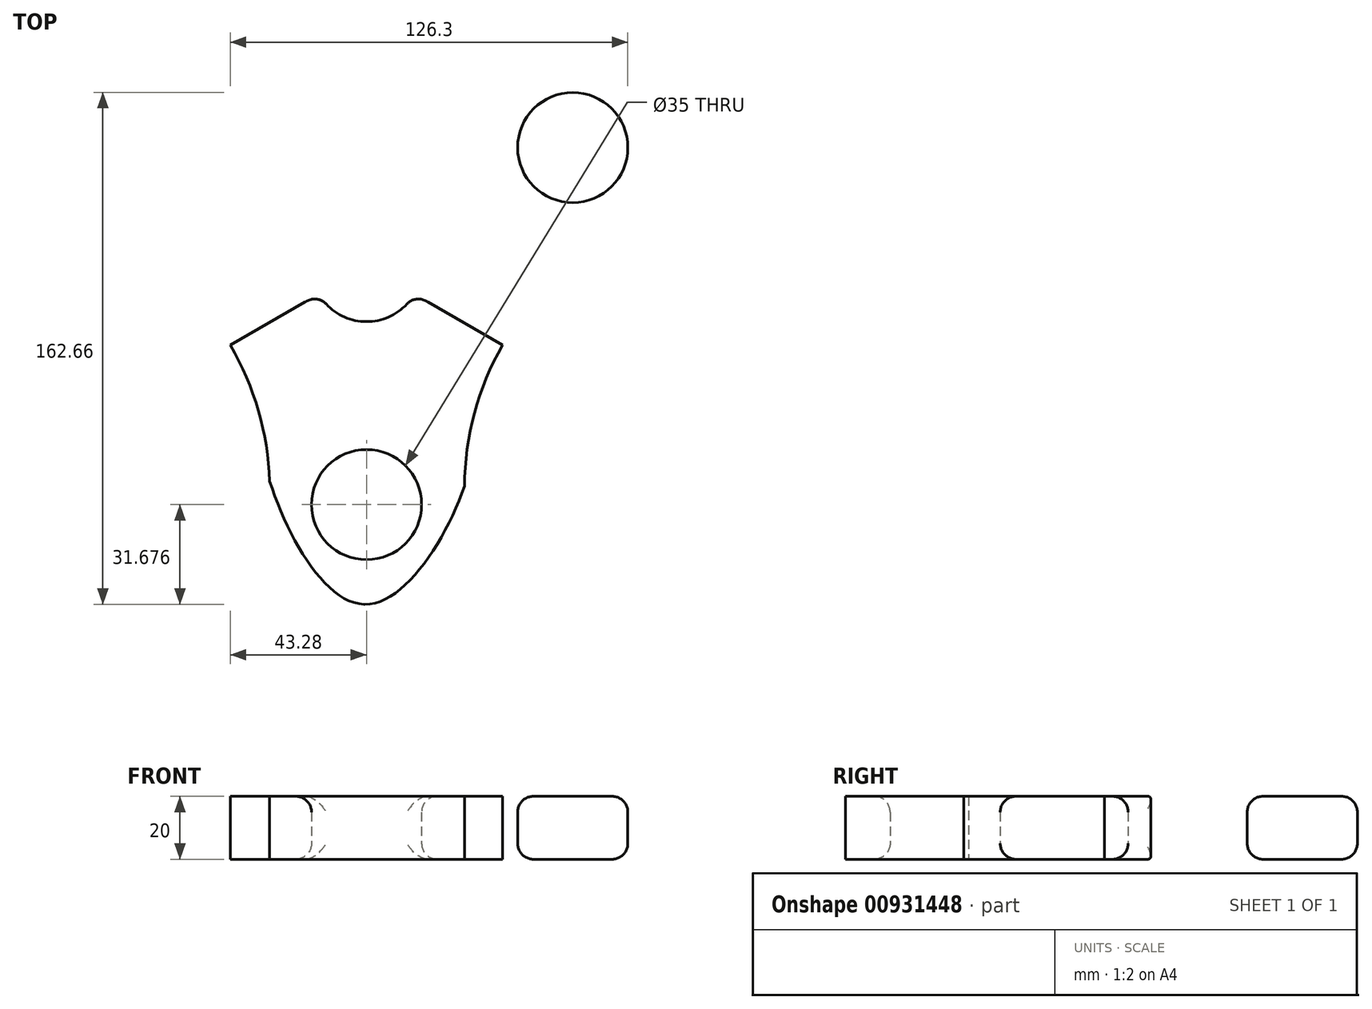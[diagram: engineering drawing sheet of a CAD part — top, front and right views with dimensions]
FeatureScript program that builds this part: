
annotation { "Feature Type Name" : "Feature", "Feature Type Description" : "" }
export const myFeature = defineFeature(function(context is Context, id is Id, definition is map)
    precondition{}
    {
        {
            var Q0;
            Q0=qCreatedBy(makeId("Top.planeOp"),FACE);
            var sketch = newSketch(context, id + "F0", { "sketchPlane" : qUnion([Q0])});
            skCircle(sketch, "E0.MirrorC", {"center": v(-65.69, 37.54) * mm, "radius": 17.5 * mm});
            skCircle(sketch, "E1", {"center": v(0, 0) * mm, "radius": 107.34 * mm});
            skArc(sketch, "E2", {"start": v(-43.65, 60.75) * mm, "mid": v(-92.55, 54.36) * mm, "end": v(-75.97, 7.92) * mm});
            skCircle(sketch, "E3.MirrorC", {"center": v(65.52, 37.83) * mm, "radius": 17.5 * mm});
            skCircle(sketch, "E4", {"center": v(0, 0) * mm, "radius": 17.5 * mm});
            skLineSegment(sketch, "E5", {"start": v(0, 0) * mm, "end": v(0, 50.1) * mm});
            skArc(sketch, "E6.MirrorCS", {"start": v(43.65, 60.75) * mm, "mid": v(92.55, 54.36) * mm, "end": v(75.97, 7.92) * mm});
            skLineSegment(sketch, "E7", {"start": v(0, 0) * mm, "end": v(92.96, -53.67) * mm});
            skLineSegment(sketch, "E8", {"start": v(0, 0) * mm, "end": v(-92.96, -53.67) * mm});
            skArc(sketch, "E9.trimOffspring", {"start": v(-43.38, -25.05) * mm, "mid": v(-57.52, -6.43) * mm, "end": v(-75.97, 7.92) * mm});
            skCircle(sketch, "E10.MirrorC", {"center": v(0, -75.65) * mm, "radius": 17.5 * mm});
            skArc(sketch, "E11", {"start": v(-30.79, -68.18) * mm, "mid": v(-43.65, -24.36) * mm, "end": v(-75.97, 7.92) * mm});
            skArc(sketch, "E12", {"start": v(-43.65, 60.75) * mm, "mid": v(0.28, 50.42) * mm, "end": v(44.14, 61.02) * mm});
            skArc(sketch, "E13", {"start": v(75.97, 7.92) * mm, "mid": v(43.25, -24.97) * mm, "end": v(31.13, -69.75) * mm});
            skArc(sketch, "E14", {"start": v(-30.79, -68.18) * mm, "mid": v(-0.8, -107.33) * mm, "end": v(31.13, -69.75) * mm});
            skFitSpline(sketch, "E15", {"points": [v(-75.97, 7.92) * mm, v(-43.38, -25.05) * mm, v(-30.79, -68.18) * mm, v(-0.8, -107.33) * mm, v(31.13, -69.75) * mm, v(43.38, -25.05) * mm, v(75.97, 7.92) * mm, v(92.96, 53.67) * mm, v(44.14, 61.02) * mm, v(0, 50.1) * mm, v(-43.65, 60.75) * mm, v(-94.93, 50.1) * mm, v(-75.97, 7.92) * mm]});
            skSolve(sketch);
        }
        {
            var Q0;
            {var subQ5=sQuery(id+"F0.wireOp",EDGE,"zdI8FKuQ-oBQZ-7qeJ-rRJp-botCcD2bO7yp");Q0=makeQuery(id+"F0.imprint","IMPRINT",FACE,{"disambiguationData":[TD([[makeQuery(id+"F0.imprint","IMPRINT",EDGE,{"derivedFrom":subQ5}),-1.0]])]});}
            var Q1;
            Q1=makeQuery(id+"F0.imprint","IMPRINT",FACE,{"disambiguationData":[TD([[makeQuery(id+"F0.imprint","IMPRINT",EDGE,{"derivedFrom":sQuery(id+"F0.wireOp",EDGE,"E3.MirrorC")}),1.0]])]});
            var Q2;
            Q2=makeQuery(id+"F0.imprint","IMPRINT",FACE,{"disambiguationData":[TD([[makeQuery(id+"F0.imprint","IMPRINT",EDGE,{"derivedFrom":sQuery(id+"F0.wireOp",EDGE,"E0.MirrorC")}),-1.0]])]});
            var Q3;
            Q3=makeQuery(id+"F0.imprint","IMPRINT",FACE,{"disambiguationData":[TD([[makeQuery(id+"F0.imprint","IMPRINT",EDGE,{"derivedFrom":sQuery(id+"F0.wireOp",EDGE,"E10.MirrorC")}),-1.0]])]});
            extrude(context, id + "F1", {"entities" : qUnion([Q0, Q1, Q2, Q3]), "depth" : 20 * mm, "offsetDistance" : 25 * mm});
        }
        {
            var Q0;
            Q0=makeQuery(id+"F1.opExtrude","SWEPT_FACE",FACE,{"disambiguationData":[OSD([sQuery(id+"F0.wireOp",EDGE,"E0.MirrorC")])]});
            var Q1;
            Q1=makeQuery(id+"F1.opExtrude","SWEPT_FACE",FACE,{"disambiguationData":[OSD([sQuery(id+"F0.wireOp",EDGE,"E4")])]});
            var Q2;
            Q2=makeQuery(id+"F1.opExtrude","SWEPT_FACE",FACE,{"disambiguationData":[OSD([sQuery(id+"F0.wireOp",EDGE,"E3.MirrorC")])]});
            var Q3;
            Q3=makeQuery(id+"F1.opExtrude","SWEPT_FACE",FACE,{"disambiguationData":[OSD([sQuery(id+"F0.wireOp",EDGE,"E10.MirrorC")])]});
            fillet(context, id + "F2", {"entities" : qUnion([Q0, Q1, Q2, Q3]), "radius" : 5 * mm, "tangentPropagation" : true, "allowEdgeOverflow" : false});
        }
    });
